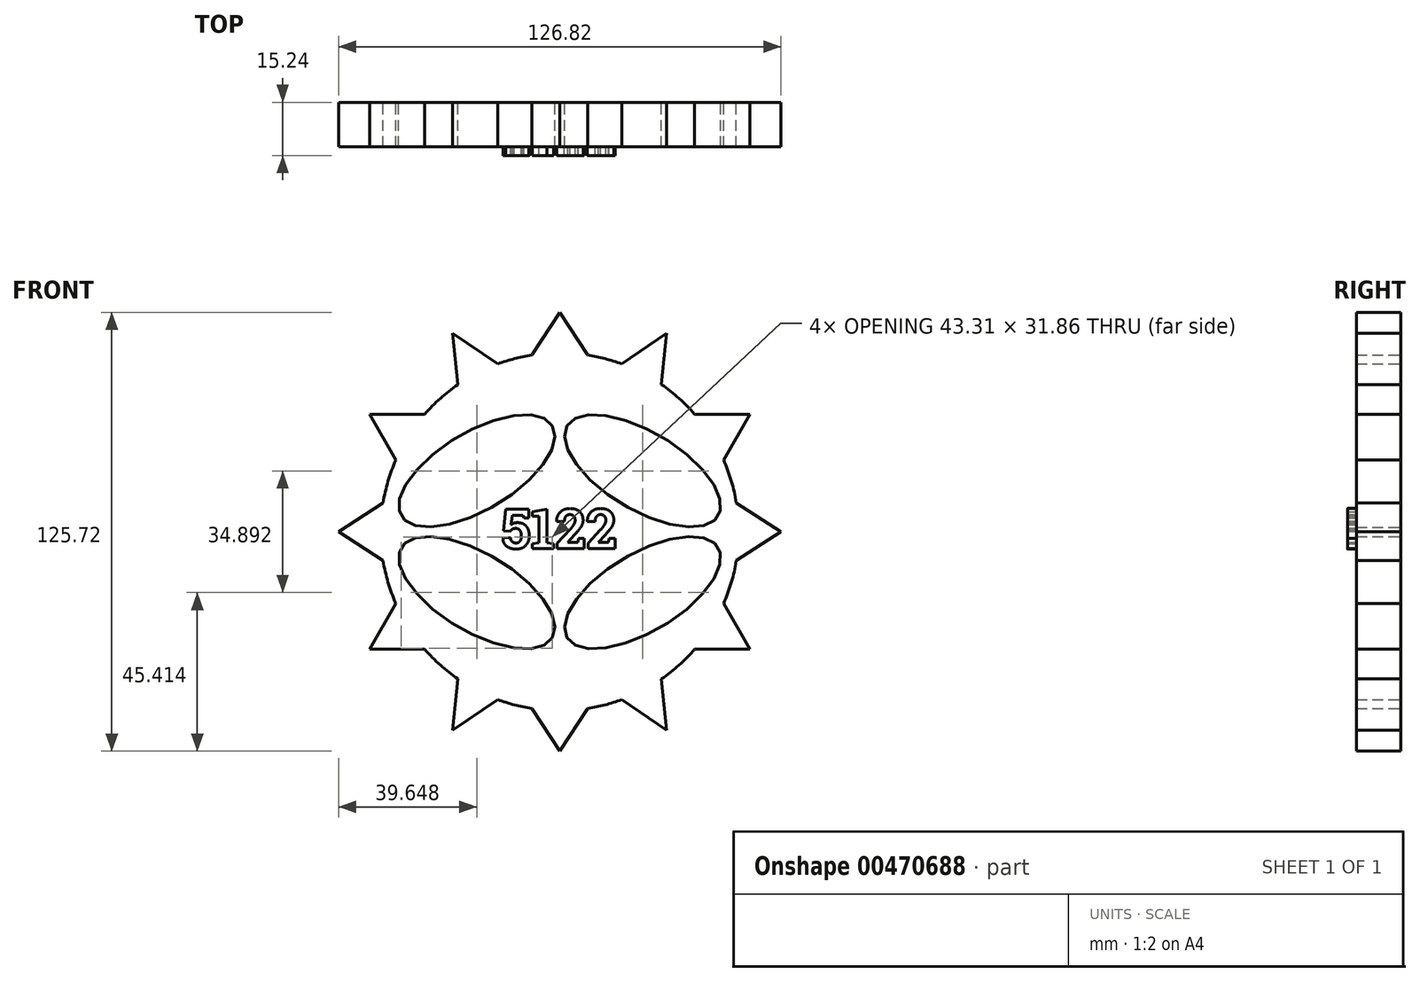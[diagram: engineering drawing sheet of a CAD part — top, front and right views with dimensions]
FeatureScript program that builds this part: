
annotation { "Feature Type Name" : "Feature", "Feature Type Description" : "" }
export const myFeature = defineFeature(function(context is Context, id is Id, definition is map)
    precondition{}
    {
        {
            var Q0;
            Q0=qCreatedBy(makeId("Front.planeOp"),FACE);
            var sketch = newSketch(context, id + "F0", { "sketchPlane" : qUnion([Q0])});
            skArc(sketch, "E0", {"start": v(-47, 20.55) * mm, "mid": v(-49.2, 14.53) * mm, "end": v(-50.62, 8.28) * mm});
            skLineSegment(sketch, "E1", {"start": v(-50.62, 8.28) * mm, "end": v(-63.41, 0) * mm});
            skLineSegment(sketch, "E2", {"start": v(-47, 20.55) * mm, "end": v(-54.44, 33.69) * mm});
            skLineSegment(sketch, "E3", {"start": v(-54.44, 33.69) * mm, "end": v(-38.68, 33.69) * mm});
            skLineSegment(sketch, "E4", {"start": v(-29.16, 42.2) * mm, "end": v(-30.68, 56.85) * mm});
            skLineSegment(sketch, "E5", {"start": v(-30.68, 56.85) * mm, "end": v(-17.75, 48.13) * mm});
            skLineSegment(sketch, "E6", {"start": v(-8.04, 50.66) * mm, "end": v(0, 62.86) * mm});
            skArc(sketch, "E7.trimOffspring", {"start": v(-29.16, 42.2) * mm, "mid": v(-34.19, 38.24) * mm, "end": v(-38.68, 33.69) * mm});
            skLineSegment(sketch, "E8.MirrorCS", {"start": v(8.04, 50.66) * mm, "end": v(0, 62.86) * mm});
            skLineSegment(sketch, "E9.MirrorCS", {"start": v(30.68, 56.85) * mm, "end": v(17.75, 48.13) * mm});
            skLineSegment(sketch, "E10.MirrorCS", {"start": v(29.16, 42.2) * mm, "end": v(30.68, 56.85) * mm});
            skLineSegment(sketch, "E11.MirrorCS", {"start": v(54.44, 33.69) * mm, "end": v(38.68, 33.69) * mm});
            skLineSegment(sketch, "E12.MirrorCS", {"start": v(47, 20.55) * mm, "end": v(54.44, 33.69) * mm});
            skLineSegment(sketch, "E13.MirrorCS", {"start": v(50.62, 8.28) * mm, "end": v(63.41, 0) * mm});
            skLineSegment(sketch, "E14.MirrorCS", {"start": v(-50.62, -8.28) * mm, "end": v(-63.41, 0) * mm});
            skLineSegment(sketch, "E15.MirrorCS", {"start": v(-47, -20.55) * mm, "end": v(-54.44, -33.69) * mm});
            skLineSegment(sketch, "E16.MirrorCS", {"start": v(-54.44, -33.69) * mm, "end": v(-38.68, -33.69) * mm});
            skLineSegment(sketch, "E17.MirrorCS", {"start": v(-29.16, -42.2) * mm, "end": v(-30.68, -56.85) * mm});
            skLineSegment(sketch, "E18.MirrorCS", {"start": v(-30.68, -56.85) * mm, "end": v(-17.75, -48.13) * mm});
            skLineSegment(sketch, "E19.MirrorCS", {"start": v(-8.04, -50.66) * mm, "end": v(0, -62.86) * mm});
            skLineSegment(sketch, "E20.MirrorCS", {"start": v(8.04, -50.66) * mm, "end": v(0, -62.86) * mm});
            skLineSegment(sketch, "E21.MirrorCS", {"start": v(30.68, -56.85) * mm, "end": v(17.75, -48.13) * mm});
            skLineSegment(sketch, "E22.MirrorCS", {"start": v(29.16, -42.2) * mm, "end": v(30.68, -56.85) * mm});
            skLineSegment(sketch, "E23.MirrorCS", {"start": v(54.44, -33.69) * mm, "end": v(38.68, -33.69) * mm});
            skLineSegment(sketch, "E24.MirrorCS", {"start": v(47, -20.55) * mm, "end": v(54.44, -33.69) * mm});
            skLineSegment(sketch, "E25.MirrorCS", {"start": v(50.62, -8.28) * mm, "end": v(63.41, 0) * mm});
            skArc(sketch, "E26.trimOffspring", {"start": v(-8.04, 50.66) * mm, "mid": v(-12.96, 49.63) * mm, "end": v(-17.75, 48.13) * mm});
            skArc(sketch, "E27.trimOffspring", {"start": v(17.75, 48.13) * mm, "mid": v(12.96, 49.63) * mm, "end": v(8.04, 50.66) * mm});
            skArc(sketch, "E28.trimOffspring", {"start": v(38.68, 33.69) * mm, "mid": v(34.19, 38.24) * mm, "end": v(29.16, 42.2) * mm});
            skArc(sketch, "E29.trimOffspring", {"start": v(50.62, 8.28) * mm, "mid": v(49.2, 14.53) * mm, "end": v(47, 20.55) * mm});
            skArc(sketch, "E30.trimOffspring", {"start": v(47, -20.55) * mm, "mid": v(49.2, -14.53) * mm, "end": v(50.62, -8.28) * mm});
            skArc(sketch, "E31.trimOffspring", {"start": v(29.16, -42.2) * mm, "mid": v(34.19, -38.24) * mm, "end": v(38.68, -33.69) * mm});
            skArc(sketch, "E32.trimOffspring", {"start": v(8.04, -50.66) * mm, "mid": v(12.96, -49.63) * mm, "end": v(17.75, -48.13) * mm});
            skArc(sketch, "E33.trimOffspring", {"start": v(-17.75, -48.13) * mm, "mid": v(-12.96, -49.63) * mm, "end": v(-8.04, -50.66) * mm});
            skArc(sketch, "E34.trimOffspring", {"start": v(-38.68, -33.69) * mm, "mid": v(-34.19, -38.24) * mm, "end": v(-29.16, -42.2) * mm});
            skArc(sketch, "E35.trimOffspring", {"start": v(-50.62, -8.28) * mm, "mid": v(-49.2, -14.53) * mm, "end": v(-47, -20.55) * mm});
            skSolve(sketch);
        }
        {
            var Q0;
            Q0 = qSketchRegion(id + "F0", true);
            extrude(context, id + "F1", {"entities" : qUnion([Q0]), "depth" : 12.7 * mm});
        }
        {
            var Q0;
            Q0=makeQuery(id+"F1.opExtrude","CAP_FACE",FACE,{"disambiguationData":[OSD([sQuery(id+"F0.wireOp",EDGE,"E0"),sQuery(id+"F0.wireOp",EDGE,"E1"),sQuery(id+"F0.wireOp",EDGE,"E2"),sQuery(id+"F0.wireOp",EDGE,"E3"),sQuery(id+"F0.wireOp",EDGE,"E4"),sQuery(id+"F0.wireOp",EDGE,"E5"),sQuery(id+"F0.wireOp",EDGE,"E6"),sQuery(id+"F0.wireOp",EDGE,"E7.trimOffspring"),sQuery(id+"F0.wireOp",EDGE,"E8.MirrorCS"),sQuery(id+"F0.wireOp",EDGE,"E9.MirrorCS"),sQuery(id+"F0.wireOp",EDGE,"E10.MirrorCS"),sQuery(id+"F0.wireOp",EDGE,"E11.MirrorCS"),sQuery(id+"F0.wireOp",EDGE,"E12.MirrorCS"),sQuery(id+"F0.wireOp",EDGE,"E13.MirrorCS"),sQuery(id+"F0.wireOp",EDGE,"E14.MirrorCS"),sQuery(id+"F0.wireOp",EDGE,"E15.MirrorCS"),sQuery(id+"F0.wireOp",EDGE,"E16.MirrorCS"),sQuery(id+"F0.wireOp",EDGE,"E17.MirrorCS"),sQuery(id+"F0.wireOp",EDGE,"E18.MirrorCS"),sQuery(id+"F0.wireOp",EDGE,"E19.MirrorCS"),sQuery(id+"F0.wireOp",EDGE,"E20.MirrorCS"),sQuery(id+"F0.wireOp",EDGE,"E21.MirrorCS"),sQuery(id+"F0.wireOp",EDGE,"E22.MirrorCS"),sQuery(id+"F0.wireOp",EDGE,"E23.MirrorCS"),sQuery(id+"F0.wireOp",EDGE,"E24.MirrorCS"),sQuery(id+"F0.wireOp",EDGE,"E25.MirrorCS"),sQuery(id+"F0.wireOp",EDGE,"E26.trimOffspring"),sQuery(id+"F0.wireOp",EDGE,"E27.trimOffspring"),sQuery(id+"F0.wireOp",EDGE,"E28.trimOffspring"),sQuery(id+"F0.wireOp",EDGE,"E29.trimOffspring"),sQuery(id+"F0.wireOp",EDGE,"E30.trimOffspring"),sQuery(id+"F0.wireOp",EDGE,"E31.trimOffspring"),sQuery(id+"F0.wireOp",EDGE,"E32.trimOffspring"),sQuery(id+"F0.wireOp",EDGE,"E33.trimOffspring"),sQuery(id+"F0.wireOp",EDGE,"E34.trimOffspring"),sQuery(id+"F0.wireOp",EDGE,"E35.trimOffspring")])],"isStart":false});
            var sketch = newSketch(context, id + "F2", { "sketchPlane" : qUnion([Q0])});
            skEllipse(sketch, "E36", {"center": v(-23.76, 17.45) * mm, "majorRadius": 25.23 * mm, "minorRadius": 11.17 * mm, "majorAxis": v(0.86, 0.51)});
            skEllipse(sketch, "E37.MirrorC", {"center": v(23.76, 17.45) * mm, "majorRadius": 25.23 * mm, "minorRadius": 11.17 * mm, "majorAxis": v(-0.86, 0.51)});
            skEllipse(sketch, "E38.MirrorC", {"center": v(-23.76, -17.45) * mm, "majorRadius": 25.23 * mm, "minorRadius": 11.17 * mm, "majorAxis": v(0.86, -0.51)});
            skEllipse(sketch, "E39.MirrorC", {"center": v(23.76, -17.45) * mm, "majorRadius": 25.23 * mm, "minorRadius": 11.17 * mm, "majorAxis": v(-0.86, -0.51)});
            skSolve(sketch);
        }
        {
            var Q0;
            Q0 = qSketchRegion(id + "F2", true);
            extrude(context, id + "F3", {"entities" : qUnion([Q0]), "operationType" : NewBodyOperationType.REMOVE, "oppositeDirection" : true, "depth" : 25.4 * mm});
        }
        {
            var Q0;
            Q0=makeQuery(id+"F1.opExtrude","CAP_FACE",FACE,{"disambiguationData":[OSD([sQuery(id+"F0.wireOp",EDGE,"E0"),sQuery(id+"F0.wireOp",EDGE,"E1"),sQuery(id+"F0.wireOp",EDGE,"E2"),sQuery(id+"F0.wireOp",EDGE,"E3"),sQuery(id+"F0.wireOp",EDGE,"E4"),sQuery(id+"F0.wireOp",EDGE,"E5"),sQuery(id+"F0.wireOp",EDGE,"E6"),sQuery(id+"F0.wireOp",EDGE,"E7.trimOffspring"),sQuery(id+"F0.wireOp",EDGE,"E8.MirrorCS"),sQuery(id+"F0.wireOp",EDGE,"E9.MirrorCS"),sQuery(id+"F0.wireOp",EDGE,"E10.MirrorCS"),sQuery(id+"F0.wireOp",EDGE,"E11.MirrorCS"),sQuery(id+"F0.wireOp",EDGE,"E12.MirrorCS"),sQuery(id+"F0.wireOp",EDGE,"E13.MirrorCS"),sQuery(id+"F0.wireOp",EDGE,"E14.MirrorCS"),sQuery(id+"F0.wireOp",EDGE,"E15.MirrorCS"),sQuery(id+"F0.wireOp",EDGE,"E16.MirrorCS"),sQuery(id+"F0.wireOp",EDGE,"E17.MirrorCS"),sQuery(id+"F0.wireOp",EDGE,"E18.MirrorCS"),sQuery(id+"F0.wireOp",EDGE,"E19.MirrorCS"),sQuery(id+"F0.wireOp",EDGE,"E20.MirrorCS"),sQuery(id+"F0.wireOp",EDGE,"E21.MirrorCS"),sQuery(id+"F0.wireOp",EDGE,"E22.MirrorCS"),sQuery(id+"F0.wireOp",EDGE,"E23.MirrorCS"),sQuery(id+"F0.wireOp",EDGE,"E24.MirrorCS"),sQuery(id+"F0.wireOp",EDGE,"E25.MirrorCS"),sQuery(id+"F0.wireOp",EDGE,"E26.trimOffspring"),sQuery(id+"F0.wireOp",EDGE,"E27.trimOffspring"),sQuery(id+"F0.wireOp",EDGE,"E28.trimOffspring"),sQuery(id+"F0.wireOp",EDGE,"E29.trimOffspring"),sQuery(id+"F0.wireOp",EDGE,"E30.trimOffspring"),sQuery(id+"F0.wireOp",EDGE,"E31.trimOffspring"),sQuery(id+"F0.wireOp",EDGE,"E32.trimOffspring"),sQuery(id+"F0.wireOp",EDGE,"E33.trimOffspring"),sQuery(id+"F0.wireOp",EDGE,"E34.trimOffspring"),sQuery(id+"F0.wireOp",EDGE,"E35.trimOffspring")])],"isStart":false});
            var sketch = newSketch(context, id + "F4", { "sketchPlane" : qUnion([Q0])});
            skText(sketch, "E40", { "text": "5122", "fontName": "RobotoSlab-Bold.ttf"});
            const initialGuessF4  = {"E40": [-0.01681, -0.00481, 1, 0, 0.01147]};
            skSetInitialGuess(sketch, initialGuessF4);
            skSolve(sketch);
        }
        {
            var Q0;
            Q0 = qSketchRegion(id + "F4", true);
            extrude(context, id + "F5", {"entities" : qUnion([Q0]), "operationType" : NewBodyOperationType.ADD, "depth" : 2.54 * mm});
        }
    });
